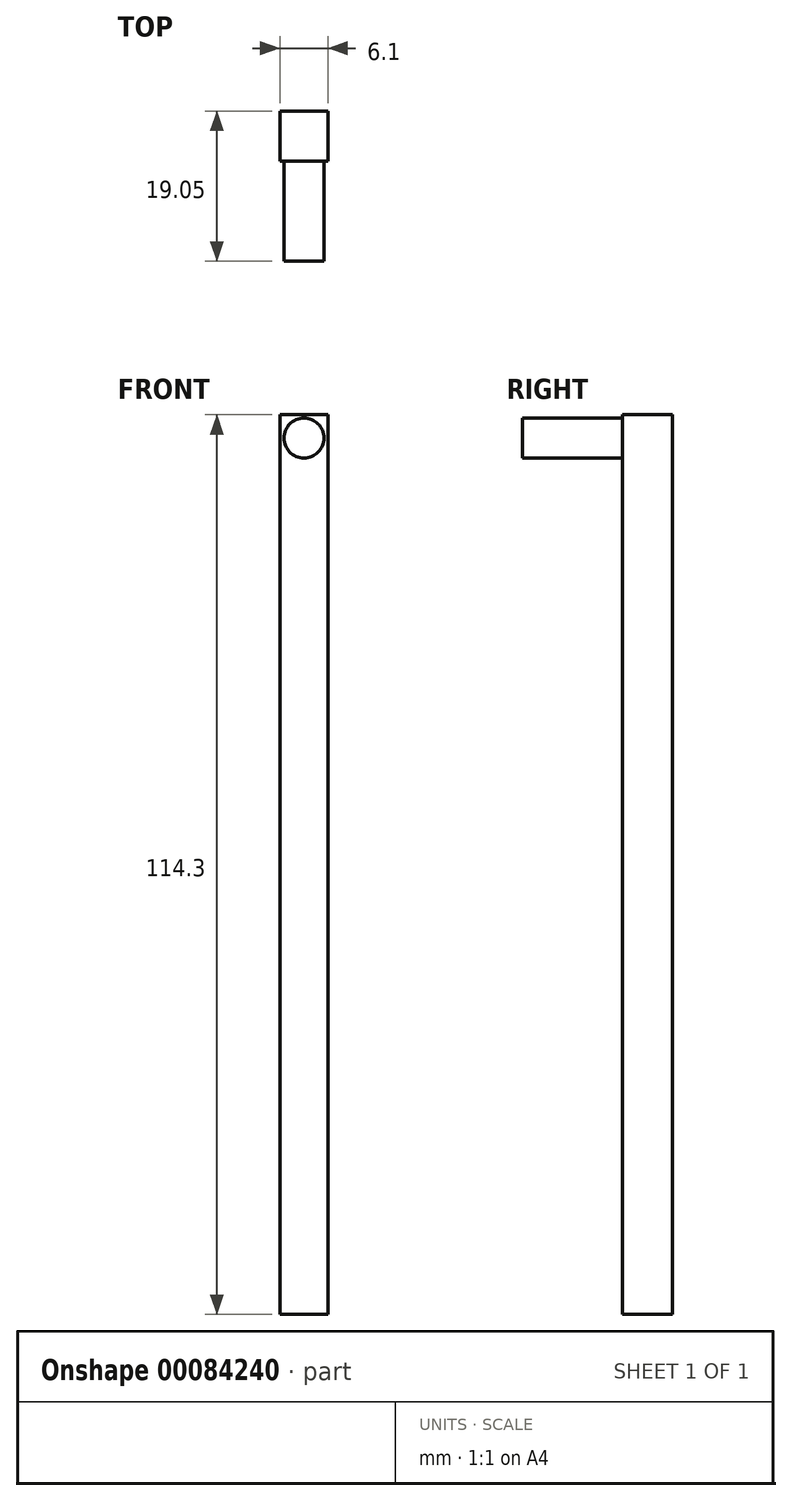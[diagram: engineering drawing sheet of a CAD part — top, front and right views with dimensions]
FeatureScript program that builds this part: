
annotation { "Feature Type Name" : "Feature", "Feature Type Description" : "" }
export const myFeature = defineFeature(function(context is Context, id is Id, definition is map)
    precondition{}
    {
        {
            var Q0;
            Q0=qCreatedBy(makeId("Front.planeOp"),FACE);
            var sketch = newSketch(context, id + "F0", { "sketchPlane" : qUnion([Q0])});
            skLineSegment(sketch, "E0.bottom", {"start": v(3.05, 57.15) * mm, "end": v(-3.05, 57.15) * mm});
            skLineSegment(sketch, "E0.top", {"start": v(3.05, -57.15) * mm, "end": v(-3.05, -57.15) * mm});
            skLineSegment(sketch, "E0.left", {"start": v(3.05, 57.15) * mm, "end": v(3.05, -57.15) * mm});
            skLineSegment(sketch, "E0.right", {"start": v(-3.05, 57.15) * mm, "end": v(-3.05, -57.15) * mm});
            skPoint(sketch, "E0.middle", {"position": v(0, 0) * mm});
            skSolve(sketch);
        }
        {
            var Q0;
            Q0=makeQuery(id+"F0.imprint","IMPRINT",FACE,{"disambiguationData":[TD([[makeQuery(id+"F0.imprint","IMPRINT",EDGE,{"derivedFrom":sQuery(id+"F0.wireOp",EDGE,"E0.bottom")}),1.0]])]});
            extrude(context, id + "F1", {"entities" : qUnion([Q0]), "endBound" : BoundingType.SYMMETRIC, "depth" : 6.35 * mm});
        }
        {
            var Q0;
            Q0=makeQuery(id+"F1.opExtrude","CAP_FACE",FACE,{"disambiguationData":[OSD([sQuery(id+"F0.wireOp",EDGE,"E0.bottom"),sQuery(id+"F0.wireOp",EDGE,"E0.top"),sQuery(id+"F0.wireOp",EDGE,"E0.left"),sQuery(id+"F0.wireOp",EDGE,"E0.right")])],"isStart":false});
            var sketch = newSketch(context, id + "F2", { "sketchPlane" : qUnion([Q0])});
            skCircle(sketch, "E1", {"center": v(0, 54.18) * mm, "radius": 2.54 * mm});
            skLineSegment(sketch, "E2", {"start": v(0, 57.15) * mm, "end": v(0, 54.18) * mm});
            skSolve(sketch);
        }
        {
            var Q0;
            Q0=makeQuery(id+"F2.imprint","IMPRINT",FACE,{"disambiguationData":[TD([[makeQuery(id+"F2.imprint","IMPRINT",EDGE,{"derivedFrom":sQuery(id+"F2.wireOp",EDGE,"E1")}),1.0]])]});
            extrude(context, id + "F3", {"entities" : qUnion([Q0]), "operationType" : NewBodyOperationType.ADD, "depth" : 12.7 * mm});
        }
    });
